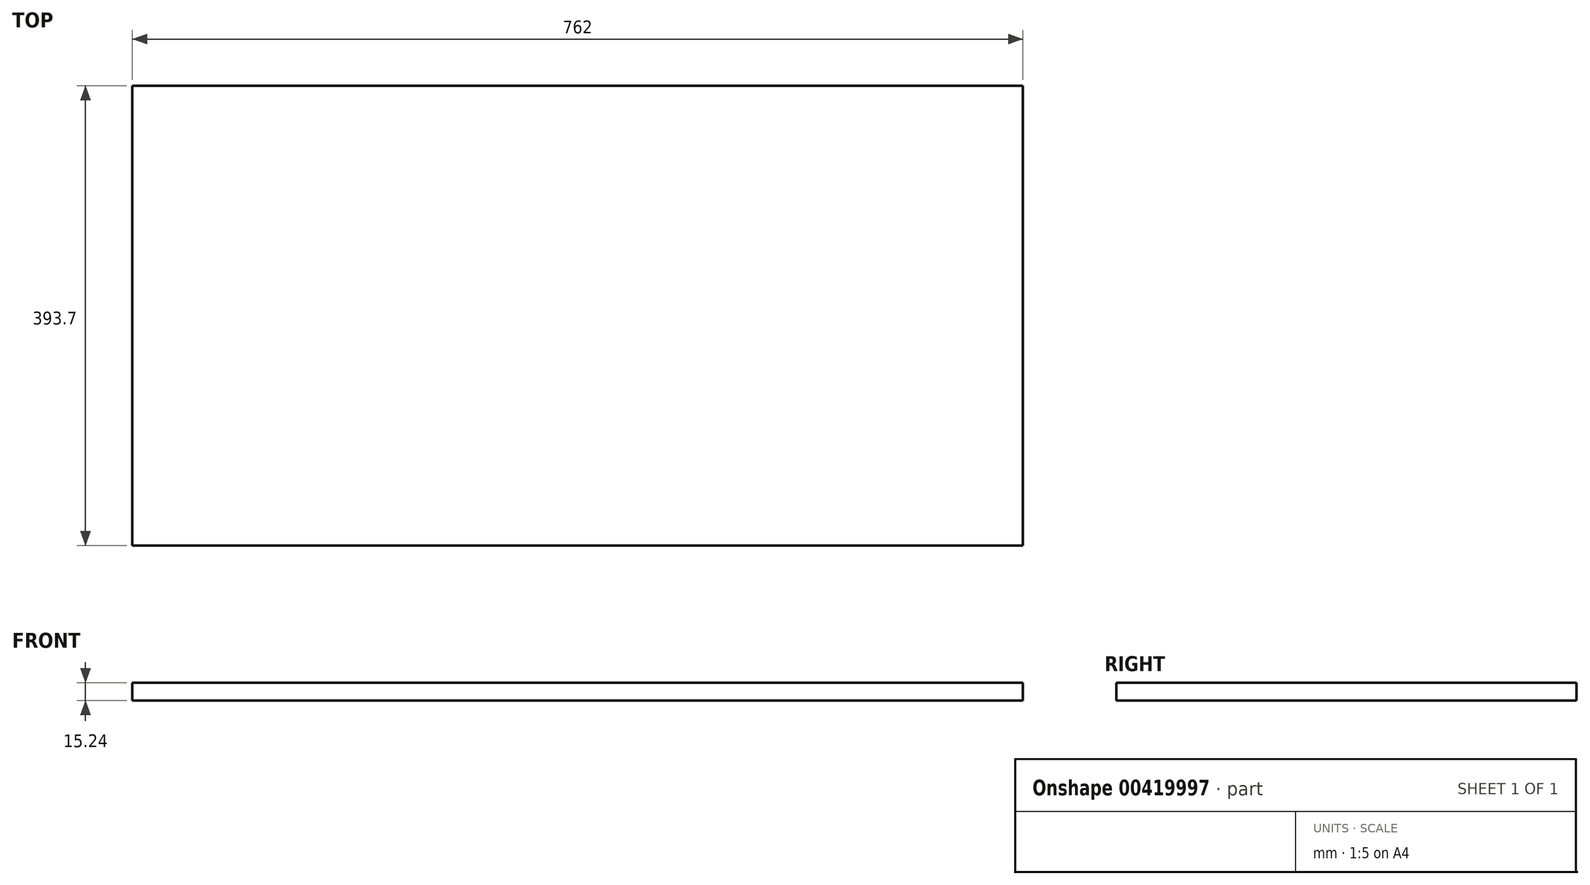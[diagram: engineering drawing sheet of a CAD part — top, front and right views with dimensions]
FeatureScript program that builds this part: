
annotation { "Feature Type Name" : "Feature", "Feature Type Description" : "" }
export const myFeature = defineFeature(function(context is Context, id is Id, definition is map)
    precondition{}
    {
        {
            var Q0;
            Q0=qCreatedBy(makeId("Top.planeOp"),FACE);
            var sketch = newSketch(context, id + "F0", { "sketchPlane" : qUnion([Q0])});
            skLineSegment(sketch, "E0.bottom", {"start": v(381, -196.85) * mm, "end": v(-381, -196.85) * mm});
            skLineSegment(sketch, "E0.top", {"start": v(381, 196.85) * mm, "end": v(-381, 196.85) * mm});
            skLineSegment(sketch, "E0.left", {"start": v(381, -196.85) * mm, "end": v(381, 196.85) * mm});
            skLineSegment(sketch, "E0.right", {"start": v(-381, -196.85) * mm, "end": v(-381, 196.85) * mm});
            skPoint(sketch, "E0.middle", {"position": v(0, 0) * mm});
            skSolve(sketch);
        }
        {
            var Q0;
            Q0=makeQuery(id+"F0.imprint","IMPRINT",FACE,{"disambiguationData":[TD([[makeQuery(id+"F0.imprint","IMPRINT",EDGE,{"derivedFrom":sQuery(id+"F0.wireOp",EDGE,"E0.bottom")}),-1.0]])]});
            extrude(context, id + "F1", {"entities" : qUnion([Q0]), "depth" : 15.24 * mm});
        }
    });
